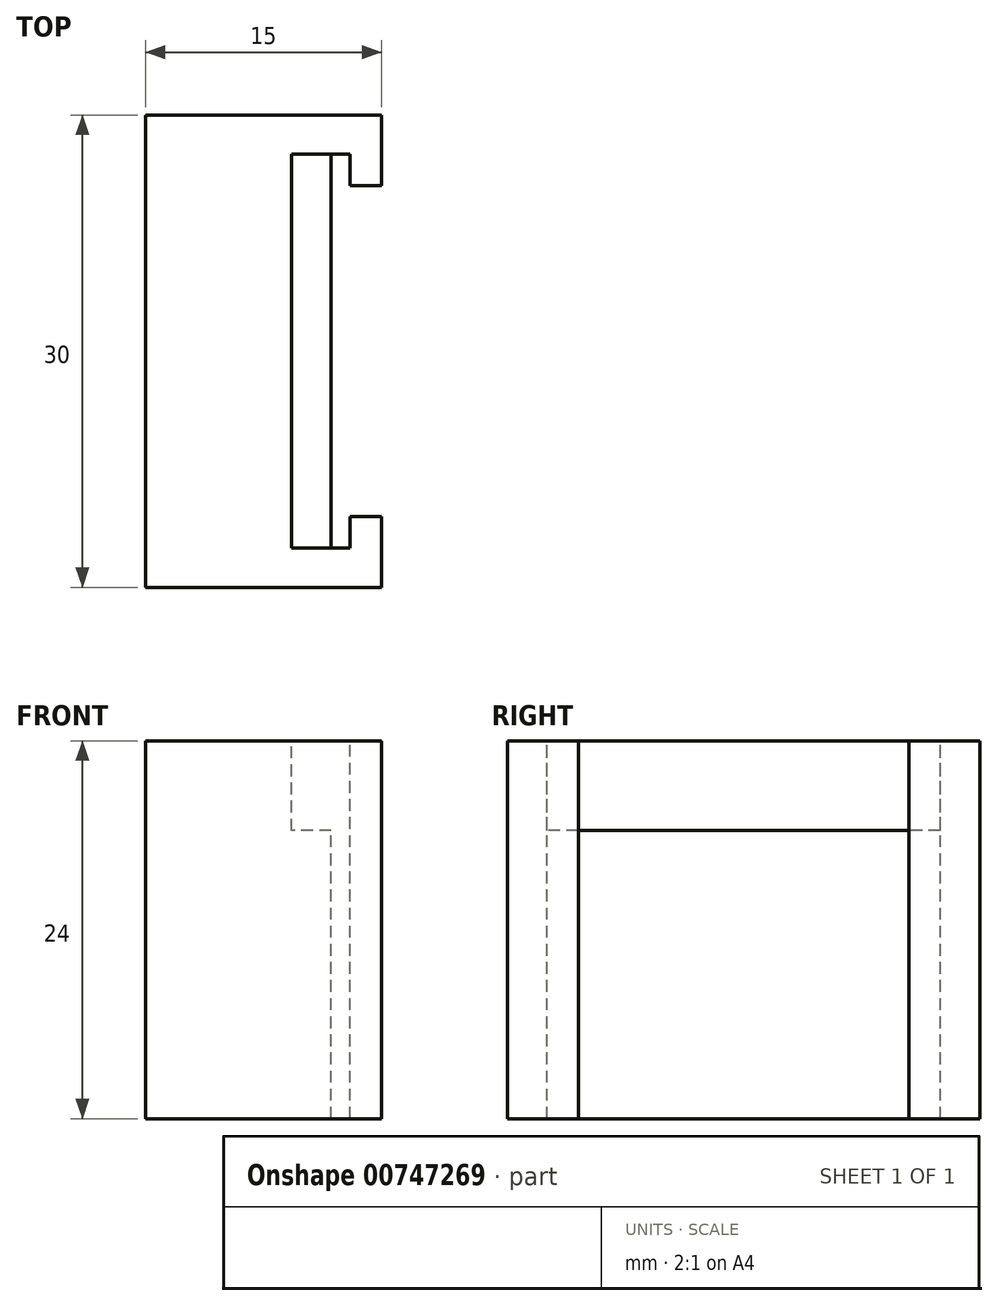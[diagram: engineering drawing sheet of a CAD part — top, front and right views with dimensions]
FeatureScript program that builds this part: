
annotation { "Feature Type Name" : "Feature", "Feature Type Description" : "" }
export const myFeature = defineFeature(function(context is Context, id is Id, definition is map)
    precondition{}
    {
        {
            var Q0;
            Q0=qCreatedBy(makeId("Front.planeOp"),FACE);
            var sketch = newSketch(context, id + "F0", { "sketchPlane" : qUnion([Q0])});
            skLineSegment(sketch, "E0.bottom", {"start": v(0, 0) * mm, "end": v(15, 0) * mm});
            skLineSegment(sketch, "E0.top", {"start": v(0, 24) * mm, "end": v(15, 24) * mm});
            skLineSegment(sketch, "E0.left", {"start": v(0, 0) * mm, "end": v(0, 24) * mm});
            skLineSegment(sketch, "E0.right", {"start": v(15, 0) * mm, "end": v(15, 24) * mm});
            skSolve(sketch);
        }
        {
            var Q0;
            Q0=qSketchRegion(id+"F0",true);
            extrude(context, id + "F1", {"entities" : qUnion([Q0]), "depth" : 30 * mm, "offsetDistance" : 25 * mm});
        }
        {
            var Q0;
            Q0=makeQuery(id+"F1.opExtrude","SWEPT_FACE",FACE,{"disambiguationData":[OSD([sQuery(id+"F0.wireOp",EDGE,"E0.top")])]});
            var sketch = newSketch(context, id + "F2", { "sketchPlane" : qUnion([Q0])});
            skLineSegment(sketch, "E1.bottom", {"start": v(11.8, -2.5) * mm, "end": v(13, -2.5) * mm});
            skLineSegment(sketch, "E1.top", {"start": v(11.8, -27.5) * mm, "end": v(13, -27.5) * mm});
            skLineSegment(sketch, "E1.left", {"start": v(11.8, -2.5) * mm, "end": v(11.8, -27.5) * mm});
            skLineSegment(sketch, "E1.right", {"start": v(13, -2.5) * mm, "end": v(13, -27.5) * mm});
            skSolve(sketch);
        }
        {
            var Q0;
            Q0=qSketchRegion(id+"F2",true);
            extrude(context, id + "F3", {"entities" : qUnion([Q0]), "operationType" : NewBodyOperationType.REMOVE, "endBound" : BoundingType.THROUGH_ALL, "oppositeDirection" : true, "depth" : 25 * mm, "offsetDistance" : 25 * mm});
        }
        {
            var Q0;
            Q0=makeQuery(id+"F1.opExtrude","SWEPT_FACE",FACE,{"disambiguationData":[OSD([sQuery(id+"F0.wireOp",EDGE,"E0.top")])]});
            var sketch = newSketch(context, id + "F4", { "sketchPlane" : qUnion([Q0])});
            skLineSegment(sketch, "E2.bottom", {"start": v(13, -4.5) * mm, "end": v(15, -4.5) * mm});
            skLineSegment(sketch, "E2.top", {"start": v(13, -25.5) * mm, "end": v(15, -25.5) * mm});
            skLineSegment(sketch, "E2.left", {"start": v(13, -4.5) * mm, "end": v(13, -25.5) * mm});
            skLineSegment(sketch, "E2.right", {"start": v(15, -4.5) * mm, "end": v(15, -25.5) * mm});
            skSolve(sketch);
        }
        {
            var Q0;
            Q0=qSketchRegion(id+"F4",true);
            extrude(context, id + "F5", {"entities" : qUnion([Q0]), "operationType" : NewBodyOperationType.REMOVE, "endBound" : BoundingType.THROUGH_ALL, "oppositeDirection" : true, "depth" : 25 * mm, "offsetDistance" : 25 * mm});
        }
        {
            var Q0;
            Q0=makeQuery(id+"F1.opExtrude","SWEPT_FACE",FACE,{"disambiguationData":[OSD([sQuery(id+"F0.wireOp",EDGE,"E0.top")])]});
            var sketch = newSketch(context, id + "F6", { "sketchPlane" : qUnion([Q0])});
            skLineSegment(sketch, "E3.bottom", {"start": v(11.8, -2.5) * mm, "end": v(9.3, -2.5) * mm});
            skLineSegment(sketch, "E3.top", {"start": v(11.8, -27.5) * mm, "end": v(9.3, -27.5) * mm});
            skLineSegment(sketch, "E3.left", {"start": v(11.8, -2.5) * mm, "end": v(11.8, -27.5) * mm});
            skLineSegment(sketch, "E3.right", {"start": v(9.3, -2.5) * mm, "end": v(9.3, -27.5) * mm});
            skSolve(sketch);
        }
        {
            var Q0;
            Q0=qSketchRegion(id+"F6",true);
            extrude(context, id + "F7", {"entities" : qUnion([Q0]), "operationType" : NewBodyOperationType.REMOVE, "oppositeDirection" : true, "depth" : 5.7 * mm, "offsetDistance" : 25 * mm});
        }
    });
